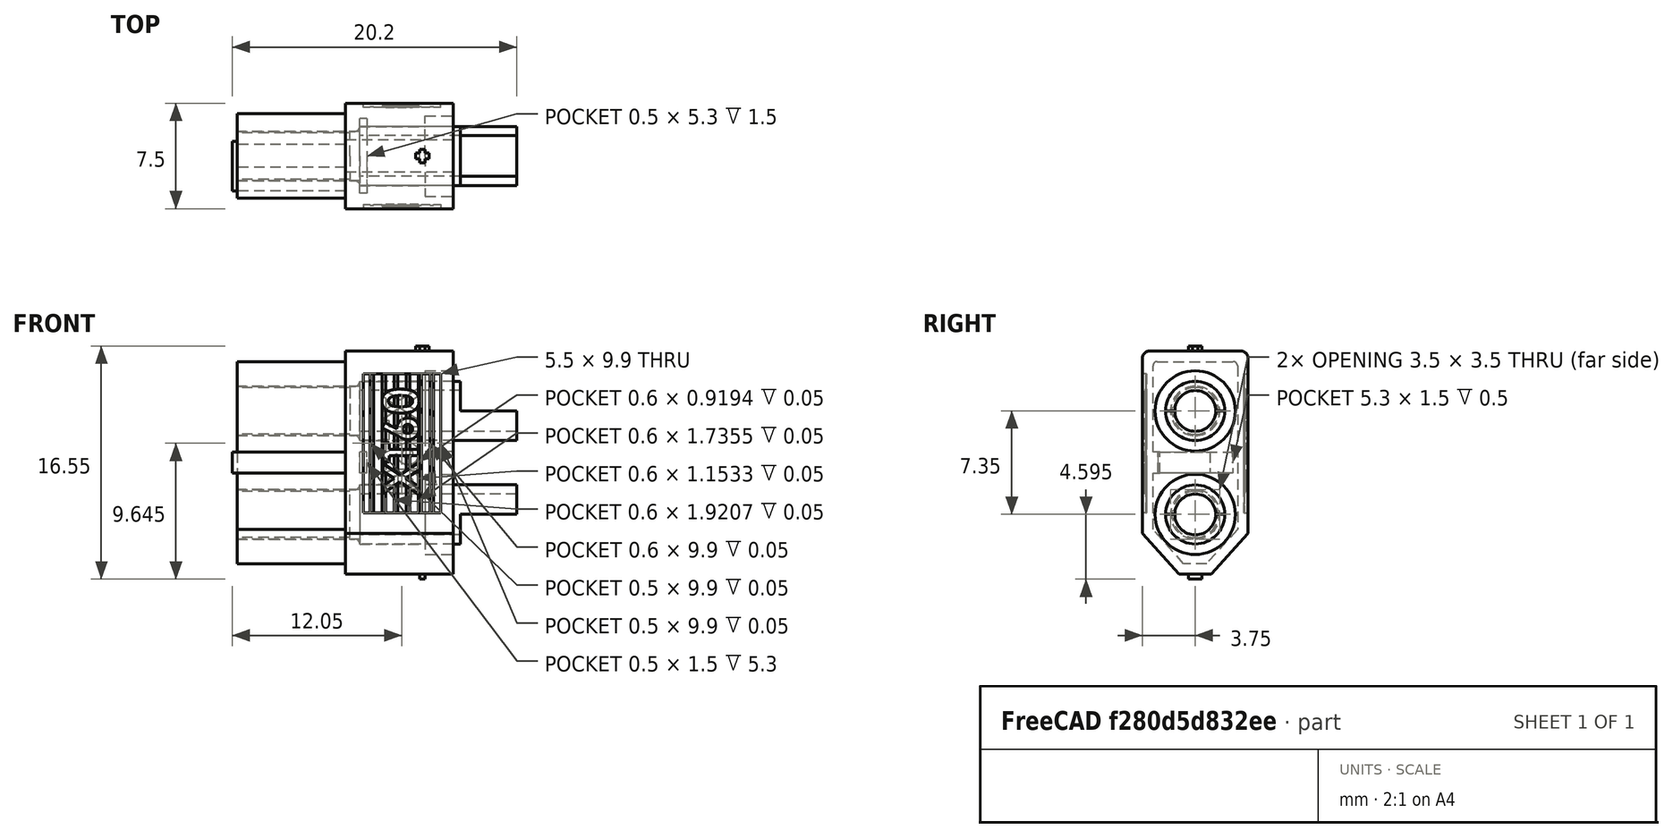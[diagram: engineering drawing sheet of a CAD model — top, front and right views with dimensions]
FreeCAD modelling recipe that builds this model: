
FCSTD DOCUMENT  (FreeCAD 0.20R29177 (Git))
Label: xt_001
License: Public Domain
LicenseURL: http://en.wikipedia.org/wiki/Public_domain
objects: Part::Feature×3, Spreadsheet::Sheet×1, Part::Compound2×1, Sketcher::SketchObject×1, PartDesign::Body×1, App::Part×1
note: 5 computed .brp shape members not serialized (recipe doc carries the construction recipe); baked Part::Feature solids carry a one-line shape summary decoded from their .brp

FEATURE [Spreadsheet::Sheet] Spreadsheet  label="xtSp"
  cells = A2=base; B2(base)=8.300000000000001; A3=haut; B3(haut)=13.25; A4=toitHaut; B4(toitHaut)=2.5; A5=fetierLarg; B5(fetierLarg)=3
FEATURE [Part::Feature] Solid
  shape: bbox 19.85 x 5.084 x 5.084 mm, 17 faces (baked)
FEATURE [Part::Feature] Solid001
  shape: bbox 19.85 x 5.084 x 5.084 mm, 17 faces (baked)
FEATURE [Part::Feature] Solid002
  shape: bbox 15.7 x 7.5 x 16.55 mm, 359 faces (baked)
FEATURE [Part::Compound2] Compound  label="XT60MaleConnector"
  Links = -> [Solid,Solid001,Solid002]
  Placement = pos=(6.2e-15,-8,6.5) rot=(-0.707107,-0.707107,0;3.14159rad)
FEATURE [Sketcher::SketchObject] Sketch
  FullyConstrained = true
  MapMode = 5
  Placement = pos=(0,0,0) rot=(1,0,0;1.5708rad)
  Support = -> [XZ_Plane001]
  expr: Constraints[13] = <<xtSp>>.base
  expr: Constraints[14] = <<xtSp>>.haut
  expr: Constraints[16] = <<xtSp>>.fetierLarg
  expr: Constraints[17] = <<xtSp>>.toitHaut
  sketch-geometry (7):
    g0: LineSegment StartX=-4.15 StartY=0 StartZ=0 EndX=-4.15 EndY=13.25 EndZ=0
    g1: LineSegment StartX=-4.15 StartY=13.25 StartZ=0 EndX=-1.5 EndY=15.75 EndZ=0
    g2: LineSegment StartX=-1.5 StartY=15.75 StartZ=0 EndX=1.5 EndY=15.75 EndZ=0
    g3: LineSegment StartX=1.5 StartY=15.75 StartZ=0 EndX=4.15 EndY=13.25 EndZ=0
    g4: LineSegment StartX=4.15 StartY=13.25 StartZ=0 EndX=4.15 EndY=0 EndZ=0
    g5: LineSegment StartX=4.15 StartY=0 StartZ=0 EndX=-4.15 EndY=0 EndZ=0
    g6: LineSegment StartX=-4.15 StartY=13.25 StartZ=0 EndX=4.15 EndY=13.25 EndZ=0
  constraints (18):
    c: PointOnObject(g0,g-1)
    c: Vertical(g0)
    c: Coincident(g0,g1)
    c: Coincident(g1,g2)
    c: Coincident(g2,g3)
    c: Coincident(g3,g4)
    c: Vertical(g4)
    c: Coincident(g4,g5)
    c: Coincident(g5,g0)
    c: Symmetric(g0,g4,g-2)
    c: Coincident(g6,g0)
    c: Coincident(g6,g3)
    c: Horizontal(g6)
    c: DistanceX(g5,g5) = 8.3
    c: DistanceY(g4,g4) = 13.25
    c: Symmetric(g1,g2,g-2)
    c: DistanceX(g2,g2) = 3
    c: DistanceY(g0,g1) = 2.5
FEATURE [PartDesign::Body] Body
  Group = -> [Sketch]
  Origin = -> Origin001
FEATURE [App::Part] Part  label="xt"
  Group = -> [Spreadsheet,Body,Solid002,Solid,Solid001,Compound]
  Origin = -> Origin
